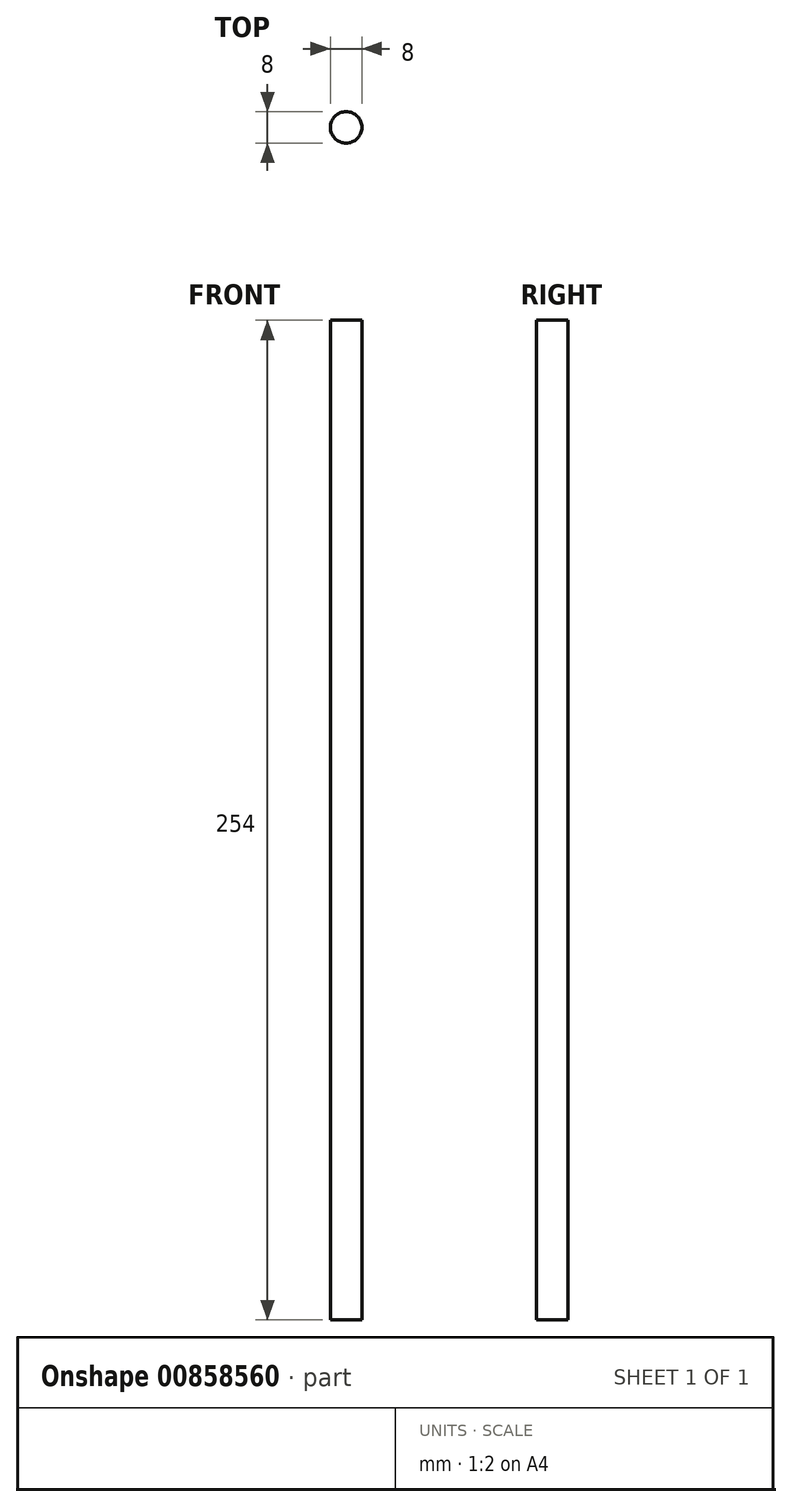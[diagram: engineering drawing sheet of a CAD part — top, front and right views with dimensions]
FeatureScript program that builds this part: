
annotation { "Feature Type Name" : "Feature", "Feature Type Description" : "" }
export const myFeature = defineFeature(function(context is Context, id is Id, definition is map)
    precondition{}
    {
        {
            var Q0;
            Q0=qCreatedBy(makeId("Top.planeOp"),FACE);
            var sketch = newSketch(context, id + "F0", { "sketchPlane" : qUnion([Q0])});
            skCircle(sketch, "E0", {"center": v(-39.35, 21.54) * mm, "radius": 4 * mm});
            skSolve(sketch);
        }
        {
            var Q0;
            Q0=makeQuery(id+"F0.imprint","IMPRINT",FACE,{"disambiguationData":[TD([[makeQuery(id+"F0.imprint","IMPRINT",EDGE,{"derivedFrom":sQuery(id+"F0.wireOp",EDGE,"E0")}),1.0]])]});
            extrude(context, id + "F1", {"entities" : qUnion([Q0]), "depth" : 254 * mm, "offsetDistance" : 25.4 * mm});
        }
    });
